# Revit family: Lighting-Suspended-Acclaim-Cylinder One HO
name_source: partatom
category: Lighting Fixtures
revit_build: Autodesk Revit 2016 (Build: 20170117_1200(x64)
units: mm (PartAtom-declared; Revit-internal decimal feet)

## family parameters
Cut with Voids When Loaded = No
Host = Face
Light Source = Yes
Part Type = Normal
Room Calculation Point = No
Round Connector Dimension = Use Diameter
Shared = No

## types (1)
- Lighting-Suspended-Acclaim-Cylinder One HO
    Apparent Load = 0 VA
    Color Filter = 16777215
    Default Elevation = 1219.2 mm  [stored 4 ft]
    Description = Suspended Cylinder
    Dimming Lamp Color Temperature Shift = <None>
    Emit Shape Visible in Rendering = No
    Emit from Circle Diameter = 152 mm  [stored 0.498688 ft]
    Height = 386 mm  [stored 1.2664 ft]
    Housing Finish = Aluminum
    Lamp = LED
    Manufacturer = Acclaim Lighting
    Model = Cylinder One HO
    Number of Poles = 1
    Photometric Web File = Load File
    Power Factor = 1
    Suspension Length = 1219.2 mm  [stored 4 ft]
    Tilt Angle = -90.00°
    URL = http://www.acclaimlighting.com
    Voltage = 0 V

note: [stored X ft] marks values corroborated as IEEE doubles in the binary element streams (Revit-internal decimal feet)

## geometry (parser evidence)
native form markers: Blend x13, Sweep x3
no freeform markers — native parametric forms only
